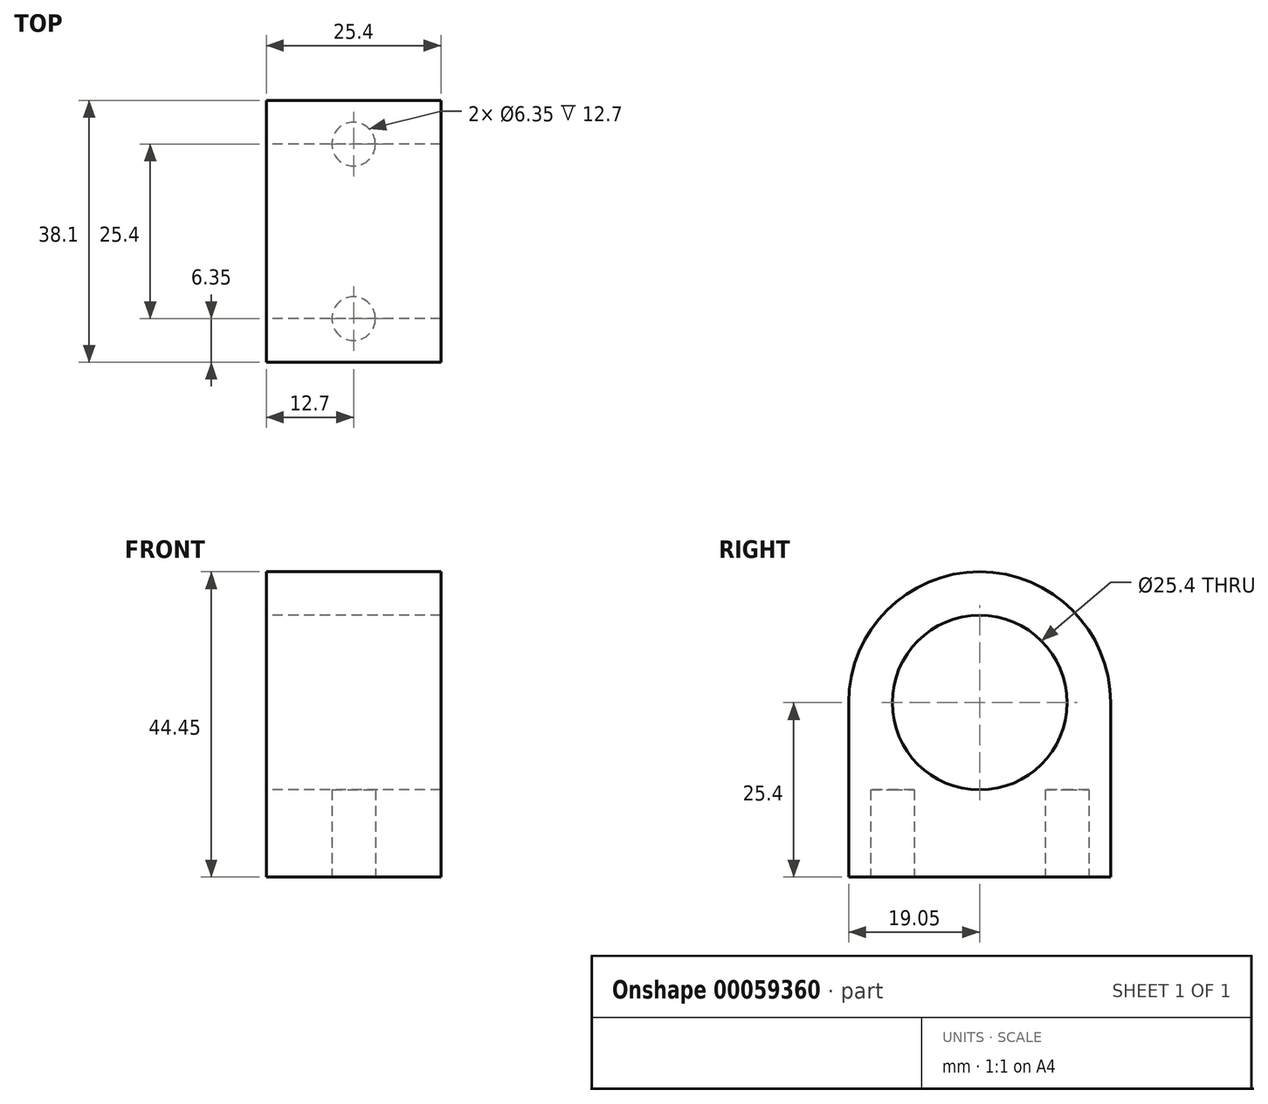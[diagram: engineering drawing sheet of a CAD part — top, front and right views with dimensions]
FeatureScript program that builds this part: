
annotation { "Feature Type Name" : "Feature", "Feature Type Description" : "" }
export const myFeature = defineFeature(function(context is Context, id is Id, definition is map)
    precondition{}
    {
        {
            var Q0;
            Q0=qCreatedBy(makeId("Right.planeOp"),FACE);
            var sketch = newSketch(context, id + "F0", { "sketchPlane" : qUnion([Q0])});
            skLineSegment(sketch, "E0", {"start": v(-39.08, 0) * mm, "end": v(39.64, 0) * mm, "construction": true});
            skLineSegment(sketch, "E1", {"start": v(0, 30.66) * mm, "end": v(0, -34.17) * mm, "construction": true});
            skArc(sketch, "E2", {"start": v(19.05, 0) * mm, "mid": v(0, 19.05) * mm, "end": v(-19.05, 0) * mm});
            skCircle(sketch, "E3", {"center": v(0, 0) * mm, "radius": 12.7 * mm});
            skLineSegment(sketch, "E4", {"start": v(-19.05, 0) * mm, "end": v(-19.05, -25.4) * mm});
            skLineSegment(sketch, "E5", {"start": v(19.05, 0) * mm, "end": v(19.05, -25.4) * mm});
            skLineSegment(sketch, "E6", {"start": v(19.05, -25.4) * mm, "end": v(-19.05, -25.4) * mm});
            skSolve(sketch);
        }
        {
            var Q0;
            Q0 = qSketchRegion(id + "F0", true);
            extrude(context, id + "F1", {"entities" : qUnion([Q0]), "endBound" : BoundingType.SYMMETRIC, "depth" : 25.4 * mm});
        }
        {
            var Q0;
            Q0=makeQuery(id+"F1.opExtrude","SWEPT_FACE",FACE,{"disambiguationData":[OSD([sQuery(id+"F0.wireOp",EDGE,"E6")])]});
            var sketch = newSketch(context, id + "F2", { "sketchPlane" : qUnion([Q0])});
            skLineSegment(sketch, "E7", {"start": v(-39.39, 0) * mm, "end": v(36.34, 0) * mm, "construction": true});
            skLineSegment(sketch, "E8", {"start": v(0, 43.86) * mm, "end": v(0, -33.2) * mm, "construction": true});
            skLineSegment(sketch, "E9", {"start": v(-22.83, 13.6) * mm, "end": v(34.82, 13.6) * mm, "construction": true});
            skLineSegment(sketch, "E10", {"start": v(-22.83, -15.89) * mm, "end": v(29.5, -15.89) * mm, "construction": true});
            skSolve(sketch);
        }
        {
            var Q0;
            {var subQ0=sQuery(id+"F0.wireOp",EDGE,"E6");Q0=makeQuery(id+"F2.imprint","IMPRINT",FACE,{"disambiguationData":[TD([[makeQuery(id+"F2.imprint","IMPRINT",EDGE,{"derivedFrom":makeQuery(id+"F1.opExtrude","CAP_EDGE",EDGE,{"disambiguationData":[OSD([subQ0])],"isStart":true})}),-1.0]])]});}
            var sketch = newSketch(context, id + "F3", { "sketchPlane" : qUnion([Q0])});
            skCircle(sketch, "E11", {"center": v(0, 12.7) * mm, "radius": 3.18 * mm});
            skCircle(sketch, "E12", {"center": v(0, -12.7) * mm, "radius": 3.18 * mm});
            skSolve(sketch);
        }
        {
            var Q0;
            Q0=makeQuery(id+"F3.imprint","IMPRINT",FACE,{"disambiguationData":[TD([[makeQuery(id+"F3.imprint","IMPRINT",EDGE,{"derivedFrom":sQuery(id+"F3.wireOp",EDGE,"E11")}),1.0]])]});
            var Q1;
            Q1=makeQuery(id+"F3.imprint","IMPRINT",FACE,{"disambiguationData":[TD([[makeQuery(id+"F3.imprint","IMPRINT",EDGE,{"derivedFrom":sQuery(id+"F3.wireOp",EDGE,"E12")}),1.0]])]});
            extrude(context, id + "F4", {"entities" : qUnion([Q0, Q1]), "operationType" : NewBodyOperationType.REMOVE, "oppositeDirection" : true, "depth" : 12.7 * mm});
        }
    });
